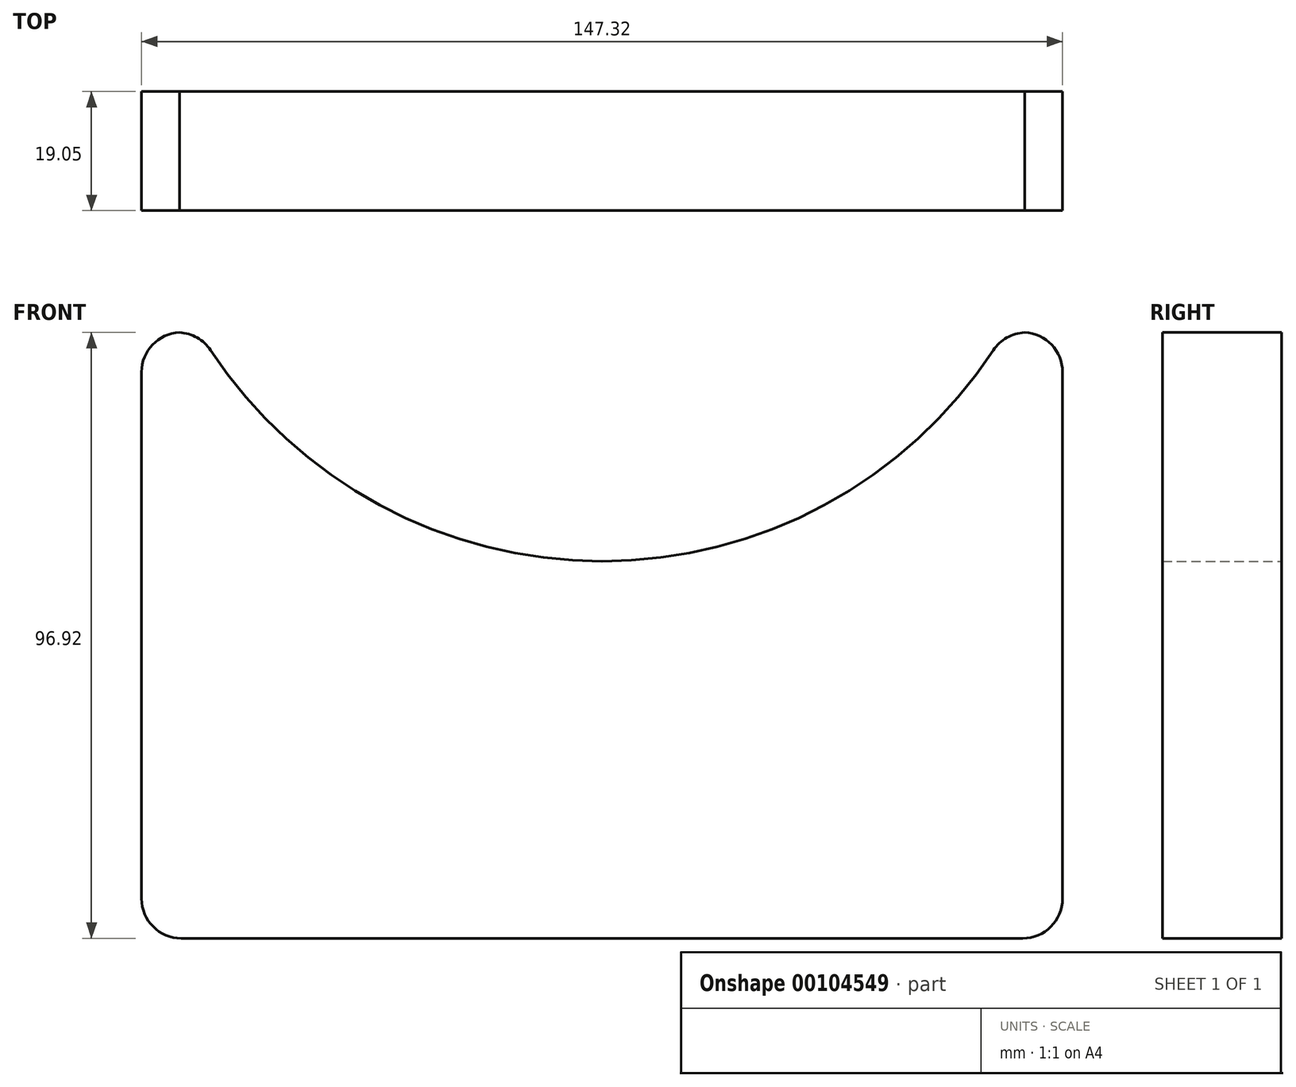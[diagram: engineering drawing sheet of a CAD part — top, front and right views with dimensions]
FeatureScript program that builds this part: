
annotation { "Feature Type Name" : "Feature", "Feature Type Description" : "" }
export const myFeature = defineFeature(function(context is Context, id is Id, definition is map)
    precondition{}
    {
        {
            var Q0;
            Q0=qCreatedBy(makeId("Front.planeOp"),FACE);
            var sketch = newSketch(context, id + "F0", { "sketchPlane" : qUnion([Q0])});
            skArc(sketch, "E0", {"start": v(-64.39, -38.32) * mm, "mid": v(0, -74.93) * mm, "end": v(64.39, -38.32) * mm});
            skLineSegment(sketch, "E1.bottom", {"start": v(73.66, -135.26) * mm, "end": v(-73.66, -135.26) * mm});
            skLineSegment(sketch, "E1.top", {"start": v(73.66, -38.32) * mm, "end": v(64.39, -38.32) * mm});
            skLineSegment(sketch, "E1.left", {"start": v(73.66, -135.25) * mm, "end": v(73.66, -38.32) * mm});
            skLineSegment(sketch, "E1.right", {"start": v(-73.66, -135.26) * mm, "end": v(-73.66, -38.32) * mm});
            skLineSegment(sketch, "E2", {"start": v(0, 0) * mm, "end": v(0, -74.93) * mm, "construction": true});
            skLineSegment(sketch, "E3.trimOffspring", {"start": v(-64.39, -38.32) * mm, "end": v(-73.66, -38.32) * mm});
            skSolve(sketch);
        }
        {
            var Q0;
            Q0=makeQuery(id+"F0.imprint","IMPRINT",FACE,{"disambiguationData":[TD([[makeQuery(id+"F0.imprint","IMPRINT",EDGE,{"derivedFrom":sQuery(id+"F0.wireOp",EDGE,"E0")}),-1.0]])]});
            extrude(context, id + "F1", {"entities" : qUnion([Q0]), "depth" : 19.05 * mm});
        }
        {
            var Q0;
            Q0=makeQuery(id+"F1.opExtrude","SWEPT_EDGE",EDGE,{"disambiguationData":[OSD([sQuery(id+"F0.wireOp",EDGE,"E1.top"),sQuery(id+"F0.wireOp",EDGE,"E1.left")])]});
            var Q1;
            Q1=makeQuery(id+"F1.opExtrude","SWEPT_EDGE",EDGE,{"disambiguationData":[OSD([sQuery(id+"F0.wireOp",EDGE,"E0"),sQuery(id+"F0.wireOp",EDGE,"E3.trimOffspring")])]});
            var Q2;
            Q2=makeQuery(id+"F1.opExtrude","SWEPT_EDGE",EDGE,{"disambiguationData":[OSD([sQuery(id+"F0.wireOp",EDGE,"E1.right"),sQuery(id+"F0.wireOp",EDGE,"E3.trimOffspring")])]});
            var Q3;
            Q3=makeQuery(id+"F1.opExtrude","SWEPT_EDGE",EDGE,{"disambiguationData":[OSD([sQuery(id+"F0.wireOp",EDGE,"E0"),sQuery(id+"F0.wireOp",EDGE,"E1.top")])]});
            var Q4;
            Q4=makeQuery(id+"F1.opExtrude","SWEPT_EDGE",EDGE,{"disambiguationData":[OSD([sQuery(id+"F0.wireOp",EDGE,"E1.bottom"),sQuery(id+"F0.wireOp",EDGE,"E1.left")])]});
            var Q5;
            Q5=makeQuery(id+"F1.opExtrude","SWEPT_EDGE",EDGE,{"disambiguationData":[OSD([sQuery(id+"F0.wireOp",EDGE,"E1.bottom"),sQuery(id+"F0.wireOp",EDGE,"E1.right")])]});
            fillet(context, id + "F2", {"entities" : qUnion([Q0, Q1, Q2, Q3, Q4, Q5]), "radius" : 6.35 * mm, "tangentPropagation" : true, "allowEdgeOverflow" : false});
        }
    });
